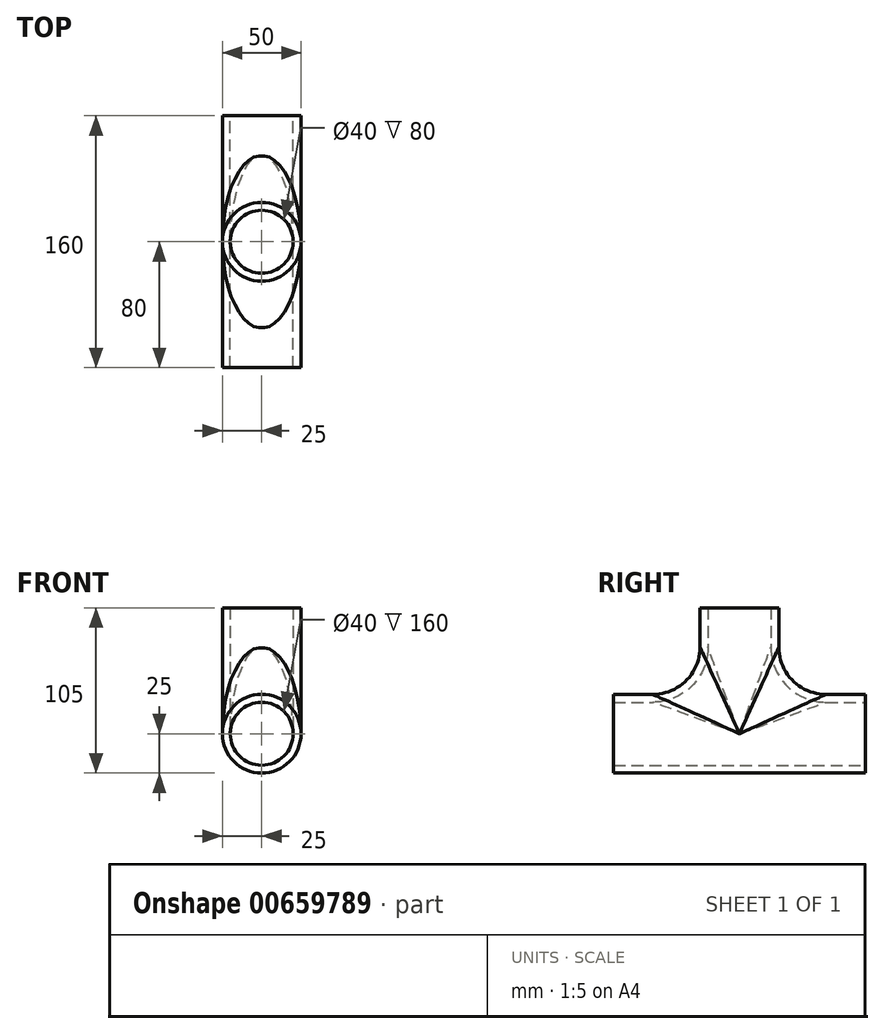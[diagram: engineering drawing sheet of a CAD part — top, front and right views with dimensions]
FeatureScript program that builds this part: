
annotation { "Feature Type Name" : "Feature", "Feature Type Description" : "" }
export const myFeature = defineFeature(function(context is Context, id is Id, definition is map)
    precondition{}
    {
        {
            var Q0;
            Q0=qCreatedBy(makeId("Front.planeOp"),FACE);
            var sketch = newSketch(context, id + "F0", { "sketchPlane" : qUnion([Q0])});
            skCircle(sketch, "E0", {"center": v(0, 0) * mm, "radius": 25 * mm});
            skSolve(sketch);
        }
        {
            var Q0;
            Q0=qCreatedBy(makeId("Top.planeOp"),FACE);
            var sketch = newSketch(context, id + "F1", { "sketchPlane" : qUnion([Q0])});
            skCircle(sketch, "E1", {"center": v(0, 0) * mm, "radius": 25 * mm});
            skSolve(sketch);
        }
        {
            var Q0;
            Q0=makeQuery(id+"F0.imprint","IMPRINT",FACE,{"disambiguationData":[TD([[makeQuery(id+"F0.imprint","IMPRINT",EDGE,{"derivedFrom":sQuery(id+"F0.wireOp",EDGE,"E0")}),1.0]])]});
            extrude(context, id + "F2", {"entities" : qUnion([Q0]), "depth" : 80 * mm, "offsetDistance" : 25 * mm, "hasSecondDirection" : true, "secondDirectionOppositeDirection" : true, "secondDirectionDepth" : 80 * mm});
        }
        {
            var Q0;
            Q0=makeQuery(id+"F1.imprint","IMPRINT",FACE,{"disambiguationData":[TD([[makeQuery(id+"F1.imprint","IMPRINT",EDGE,{"derivedFrom":sQuery(id+"F1.wireOp",EDGE,"E1")}),1.0]])]});
            extrude(context, id + "F3", {"entities" : qUnion([Q0]), "operationType" : NewBodyOperationType.ADD, "depth" : 80 * mm, "offsetDistance" : 25 * mm});
        }
        {
            var Q0;
            Q0=makeQuery(id+"F3.boolean.opBoolean","INTERSECT",EDGE,{"disambiguationData":[OD(0.0)],"derivedFrom":[makeQuery(id+"F2.opExtrude","SWEPT_FACE",FACE,{"disambiguationData":[OSD([sQuery(id+"F0.wireOp",EDGE,"E0")])]}),makeQuery(id+"F3.opExtrude","SWEPT_FACE",FACE,{"disambiguationData":[OSD([sQuery(id+"F1.wireOp",EDGE,"E1")])]})]});
            var Q1;
            Q1=makeQuery(id+"F3.boolean.opBoolean","INTERSECT",EDGE,{"disambiguationData":[OD(1.0)],"derivedFrom":[makeQuery(id+"F2.opExtrude","SWEPT_FACE",FACE,{"disambiguationData":[OSD([sQuery(id+"F0.wireOp",EDGE,"E0")])]}),makeQuery(id+"F3.opExtrude","SWEPT_FACE",FACE,{"disambiguationData":[OSD([sQuery(id+"F1.wireOp",EDGE,"E1")])]})]});
            fillet(context, id + "F4", {"entities" : qUnion([Q0, Q1]), "radius" : 30 * mm, "tangentPropagation" : true, "allowEdgeOverflow" : false});
        }
        {
            var Q0;
            Q0=makeQuery(id+"F2.opExtrude","CAP_FACE",FACE,{"disambiguationData":[OSD([sQuery(id+"F0.wireOp",EDGE,"E0")])],"isStart":false});
            var Q1;
            Q1=makeQuery(id+"F2.opExtrude","CAP_FACE",FACE,{"disambiguationData":[OSD([sQuery(id+"F0.wireOp",EDGE,"E0")])],"isStart":true});
            var Q2;
            Q2=makeQuery(id+"F3.opExtrude","CAP_FACE",FACE,{"disambiguationData":[OSD([sQuery(id+"F1.wireOp",EDGE,"E1")])],"isStart":false});
            var Q3;
            Q3=makeQuery(id+"F2.opExtrude","SWEPT_BODY",BODY,{"disambiguationData":[OSD([sQuery(id+"F0.wireOp",EDGE,"E0")])]});
            shell(context, id + "F5", {"entities" : qUnion([Q0, Q1, Q2]), "parts" : qUnion([Q3]), "thickness" : 5 * mm});
        }
    });
